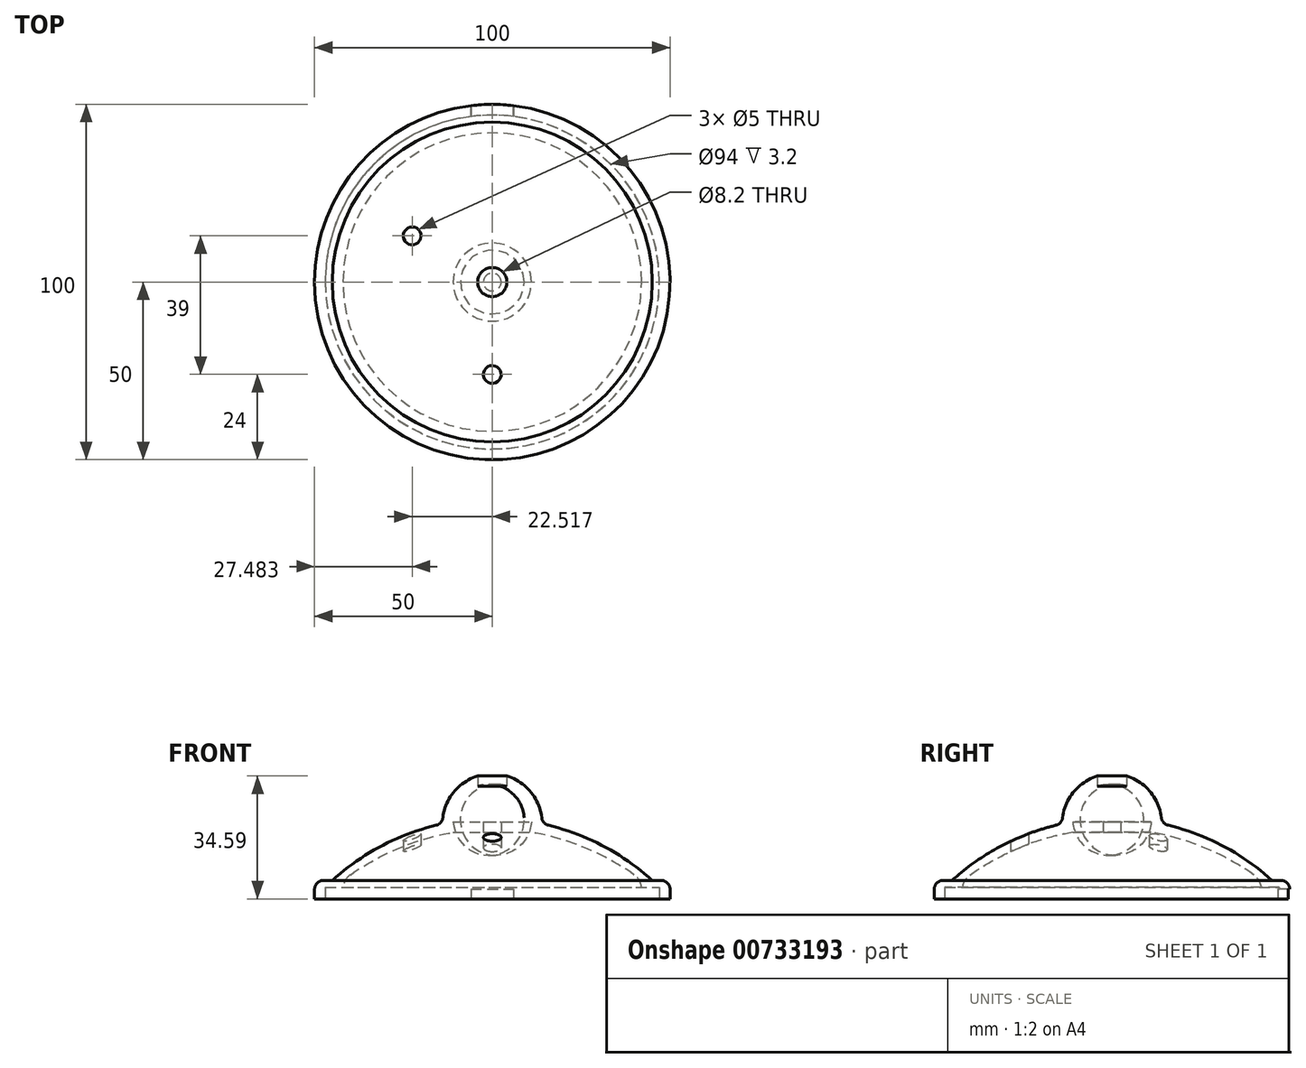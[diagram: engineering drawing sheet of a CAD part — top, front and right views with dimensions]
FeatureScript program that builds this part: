
annotation { "Feature Type Name" : "Feature", "Feature Type Description" : "" }
export const myFeature = defineFeature(function(context is Context, id is Id, definition is map)
    precondition{}
    {
        {
            var Q0;
            Q0=qCreatedBy(makeId("Right.planeOp"),FACE);
            var sketch = newSketch(context, id + "F0", { "sketchPlane" : qUnion([Q0])});
            skArc(sketch, "E0", {"start": v(-47, 0) * mm, "mid": v(-24.82, -11.62) * mm, "end": v(0, -15) * mm});
            skLineSegment(sketch, "E1", {"start": v(-47, 0) * mm, "end": v(-42, 0) * mm});
            skLineSegment(sketch, "E2", {"start": v(-42, 0) * mm, "end": v(-42, 2) * mm});
            skLineSegment(sketch, "E3", {"start": v(-42, 2) * mm, "end": v(-47, 2) * mm});
            skLineSegment(sketch, "E4", {"start": v(-47, 2) * mm, "end": v(-47, 4) * mm});
            skLineSegment(sketch, "E5", {"start": v(-47, 4) * mm, "end": v(-42, 4) * mm});
            skLineSegment(sketch, "E6", {"start": v(-42, 4) * mm, "end": v(-42, 6) * mm});
            skLineSegment(sketch, "E7", {"start": v(-45, 6) * mm, "end": v(-50, 6) * mm});
            skLineSegment(sketch, "E8", {"start": v(-50, 6) * mm, "end": v(-50, 0) * mm});
            skArc(sketch, "E9", {"start": v(-50, 0) * mm, "mid": v(-26.7, -13.74) * mm, "end": v(0, -18) * mm});
            skLineSegment(sketch, "E10", {"start": v(0, -15) * mm, "end": v(0, -18) * mm});
            skLineSegment(sketch, "E11", {"start": v(0, 0) * mm, "end": v(0, -18) * mm, "construction": true});
            skArc(sketch, "E12", {"start": v(-11, 19.5) * mm, "mid": v(-27.33, 14.65) * mm, "end": v(-42, 6) * mm});
            skArc(sketch, "E13", {"start": v(-14, 21.93) * mm, "mid": v(-30.55, 16.01) * mm, "end": v(-45, 6) * mm});
            skLineSegment(sketch, "E14", {"start": v(0, 33) * mm, "end": v(0, 36) * mm});
            skArc(sketch, "E15", {"start": v(0, 36) * mm, "mid": v(-9.93, 31.87) * mm, "end": v(-14, 21.93) * mm});
            skArc(sketch, "E16", {"start": v(0, 33) * mm, "mid": v(-7.92, 30.29) * mm, "end": v(-11, 22.5) * mm});
            skLineSegment(sketch, "E17", {"start": v(-11, 22.5) * mm, "end": v(-2.5, 22.5) * mm});
            skLineSegment(sketch, "E18", {"start": v(-11, 19.5) * mm, "end": v(-2.5, 19.5) * mm});
            skLineSegment(sketch, "E19", {"start": v(-2.5, 22.5) * mm, "end": v(-2.5, 19.5) * mm});
            skPoint(sketch, "E20.endSnap0", {"position": v(-50, 3) * mm});
            skPoint(sketch, "E20.end.orphan", {"position": v(-50, 2) * mm});
            skLineSegment(sketch, "E21", {"start": v(-47, 2) * mm, "end": v(-47, 0.8) * mm});
            skLineSegment(sketch, "E22", {"start": v(-47, 0.8) * mm, "end": v(-50, 0.8) * mm});
            skSolve(sketch);
        }
        {
            var Q0;
            Q0=makeQuery(id+"F0.imprint","IMPRINT",FACE,{"disambiguationData":[TD([[makeQuery(id+"F0.imprint","IMPRINT",EDGE,{"derivedFrom":sQuery(id+"F0.wireOp",EDGE,"E4")}),1.0]])]});
            var Q1;
            Q1=sQuery(id+"F0.wireOp",EDGE,"E11");
            revolve(context, id + "F1", {"surfaceOperationType" : NewSurfaceOperationType.NEW, "entities" : qUnion([Q0]), "axis" : qUnion([Q1]), "revolveType" : RevolveType.ONE_DIRECTION, "oppositeDirection" : true, "angle" : 360 * degree});
        }
        {
            var Q0;
            Q0=qCreatedBy(makeId("Top.planeOp"),FACE);
            var sketch = newSketch(context, id + "F2", { "sketchPlane" : qUnion([Q0])});
            skCircle(sketch, "E23", {"center": v(0, 0) * mm, "radius": 20 * mm});
            skSolve(sketch);
        }
        {
            var Q0;
            Q0=makeQuery(id+"F2.imprint","IMPRINT",FACE,{"disambiguationData":[TD([[makeQuery(id+"F2.imprint","IMPRINT",EDGE,{"derivedFrom":sQuery(id+"F2.wireOp",EDGE,"E23")}),1.0]])]});
            extrude(context, id + "F3", {"entities" : qUnion([Q0]), "operationType" : NewBodyOperationType.REMOVE, "oppositeDirection" : true, "depth" : 25 * mm, "offsetDistance" : 25 * mm});
        }
        {
            var Q0;
            Q0=qCreatedBy(makeId("Top.planeOp"),FACE);
            var sketch = newSketch(context, id + "F4", { "sketchPlane" : qUnion([Q0])});
            skCircle(sketch, "E24", {"center": v(0, -26) * mm, "radius": 2.5 * mm});
            skCircle(sketch, "E25", {"center": v(-22.52, 13) * mm, "radius": 2.5 * mm});
            skLineSegment(sketch, "E26", {"start": v(0, 0) * mm, "end": v(-22.52, 13) * mm, "construction": true});
            skCircle(sketch, "E27.MirrorC", {"center": v(22.52, 13) * mm, "radius": 2.5 * mm});
            skSolve(sketch);
        }
        {
            var Q0;
            Q0=makeQuery(id+"F4.imprint","IMPRINT",FACE,{"disambiguationData":[TD([[makeQuery(id+"F4.imprint","IMPRINT",EDGE,{"derivedFrom":sQuery(id+"F4.wireOp",EDGE,"E24")}),1.0]])]});
            var Q1;
            Q1=makeQuery(id+"F4.imprint","IMPRINT",FACE,{"disambiguationData":[TD([[makeQuery(id+"F4.imprint","IMPRINT",EDGE,{"derivedFrom":sQuery(id+"F4.wireOp",EDGE,"E25")}),1.0]])]});
            var Q2;
            Q2=makeQuery(id+"F4.imprint","IMPRINT",FACE,{"disambiguationData":[TD([[makeQuery(id+"F4.imprint","IMPRINT",EDGE,{"derivedFrom":sQuery(id+"F4.wireOp",EDGE,"E27.MirrorC")}),-1.0]])]});
            extrude(context, id + "F5", {"entities" : qUnion([Q0, Q1, Q2]), "operationType" : NewBodyOperationType.REMOVE, "depth" : 25 * mm, "offsetDistance" : 25 * mm});
        }
        {
            var Q0;
            Q0=makeQuery(id+"F1.opRevolve","SWEPT_EDGE",EDGE,{"disambiguationData":[OSD([sQuery(id+"F0.wireOp",EDGE,"E0"),sQuery(id+"F0.wireOp",EDGE,"E1")])]});
            var Q1;
            Q1=makeQuery(id+"F1.opRevolve","SWEPT_EDGE",EDGE,{"disambiguationData":[OSD([sQuery(id+"F0.wireOp",EDGE,"E6"),sQuery(id+"F0.wireOp",EDGE,"E12")])]});
            fillet(context, id + "F6", {"entities" : qUnion([Q0, Q1]), "radius" : 5 * mm, "tangentPropagation" : true, "allowEdgeOverflow" : false});
        }
        {
            var Q0;
            Q0=qCreatedBy(makeId("Front.planeOp"),FACE);
            var sketch = newSketch(context, id + "F7", { "sketchPlane" : qUnion([Q0])});
            skLineSegment(sketch, "E28.bottom", {"start": v(-6, 3.6) * mm, "end": v(6, 3.6) * mm});
            skLineSegment(sketch, "E28.top", {"start": v(-6, -3) * mm, "end": v(6, -3) * mm});
            skLineSegment(sketch, "E28.left", {"start": v(-6, 3.6) * mm, "end": v(-6, -3) * mm});
            skLineSegment(sketch, "E28.right", {"start": v(6, 3.6) * mm, "end": v(6, -3) * mm});
            skPoint(sketch, "E29.right.end.orphan", {"position": v(5, 0) * mm});
            skSolve(sketch);
        }
        {
            var Q0;
            Q0=makeQuery(id+"F7.imprint","IMPRINT",FACE,{"disambiguationData":[TD([[makeQuery(id+"F7.imprint","IMPRINT",EDGE,{"derivedFrom":sQuery(id+"F7.wireOp",EDGE,"PHSBLFIY-TZuw-bhm2-DLcI-erlKNIHIbNUr.bottom")}),-1.0]])]});
            var Q1;
            Q1=makeQuery(id+"F7.imprint","IMPRINT",FACE,{"disambiguationData":[TD([[makeQuery(id+"F7.imprint","IMPRINT",EDGE,{"derivedFrom":sQuery(id+"F7.wireOp",EDGE,"PHSBLFIY-TZuw-bhm2-DLcI-erlKNIHIbNUr.right")}),-1.0]])]});
            var Q2;
            Q2=makeQuery(id+"F7.imprint","IMPRINT",FACE,{"disambiguationData":[TD([[makeQuery(id+"F7.imprint","IMPRINT",EDGE,{"derivedFrom":sQuery(id+"F7.wireOp",EDGE,"E28.bottom")}),-1.0]])]});
            extrude(context, id + "F8", {"entities" : qUnion([Q0, Q1, Q2]), "operationType" : NewBodyOperationType.REMOVE, "oppositeDirection" : true, "depth" : 60 * mm, "offsetDistance" : 25 * mm});
        }
        {
            var Q0;
            Q0=makeQuery(id+"F1.opRevolve","SWEPT_FACE",FACE,{"disambiguationData":[OSD([sQuery(id+"F0.wireOp",EDGE,"E17")])]});
            var sketch = newSketch(context, id + "F9", { "sketchPlane" : qUnion([Q0])});
            skCircle(sketch, "E30", {"center": v(0, 0) * mm, "radius": 4.1 * mm});
            skSolve(sketch);
        }
        {
            var Q0;
            {var subQ1=sQuery(id+"F0.wireOp",EDGE,"E17");var subQ6=makeQuery(id+"F1.opRevolve","SWEPT_EDGE",EDGE,{"disambiguationData":[OSD([subQ1,sQuery(id+"F0.wireOp",EDGE,"E19")])]});Q0=makeQuery(id+"F9.imprint","IMPRINT",FACE,{"disambiguationData":[TD([[makeQuery(id+"F9.imprint","IMPRINT",EDGE,{"derivedFrom":subQ6}),1.0]])]});}
            var Q1;
            {var subQ1=sQuery(id+"F0.wireOp",EDGE,"E17");var subQ6=makeQuery(id+"F1.opRevolve","SWEPT_EDGE",EDGE,{"disambiguationData":[OSD([subQ1,sQuery(id+"F0.wireOp",EDGE,"E19")])]});Q1=makeQuery(id+"F9.imprint","IMPRINT",FACE,{"disambiguationData":[TD([[makeQuery(id+"F9.imprint","IMPRINT",EDGE,{"derivedFrom":subQ6}),-1.0]])]});}
            extrude(context, id + "F10", {"entities" : qUnion([Q0, Q1]), "operationType" : NewBodyOperationType.REMOVE, "depth" : 15 * mm, "offsetDistance" : 25 * mm});
        }
        {
            var Q0;
            Q0=makeQuery(id+"F1.opRevolve","SWEPT_EDGE",EDGE,{"disambiguationData":[OSD([sQuery(id+"F0.wireOp",EDGE,"E13"),sQuery(id+"F0.wireOp",EDGE,"E15")])]});
            var Q1;
            Q1=makeQuery(id+"F1.opRevolve","SWEPT_EDGE",EDGE,{"disambiguationData":[OSD([sQuery(id+"F0.wireOp",EDGE,"E7"),sQuery(id+"F0.wireOp",EDGE,"E8")])]});
            fillet(context, id + "F11", {"entities" : qUnion([Q0, Q1]), "radius" : 2.5 * mm, "tangentPropagation" : true, "allowEdgeOverflow" : false});
        }
    });
